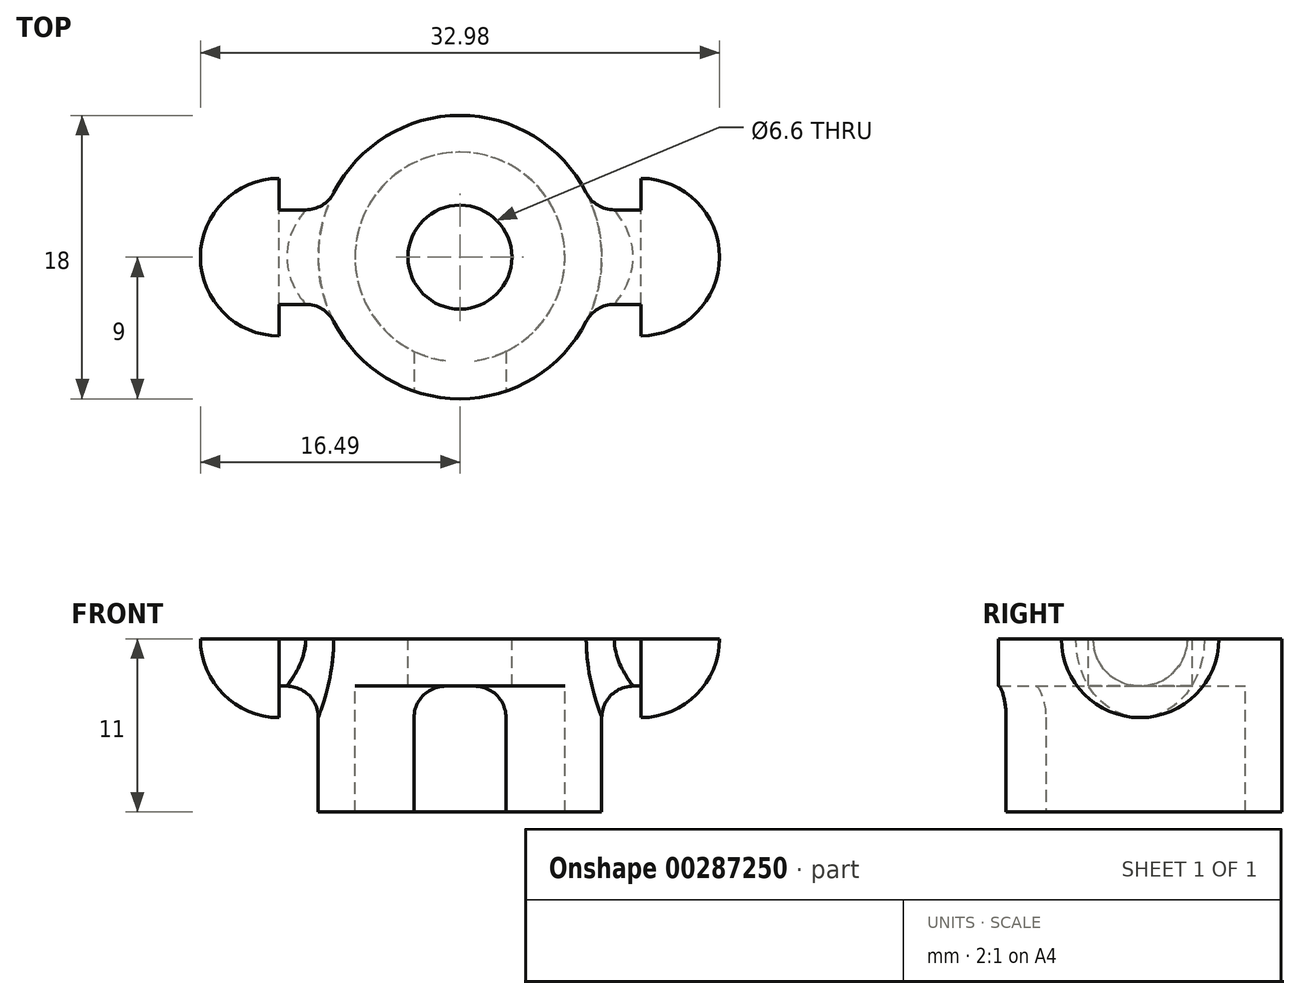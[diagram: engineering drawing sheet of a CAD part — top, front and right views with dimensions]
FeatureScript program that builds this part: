
annotation { "Feature Type Name" : "Feature", "Feature Type Description" : "" }
export const myFeature = defineFeature(function(context is Context, id is Id, definition is map)
    precondition{}
    {
        {
            var Q0;
            Q0=qCreatedBy(makeId("Front.planeOp"),FACE);
            var sketch = newSketch(context, id + "F0", { "sketchPlane" : qUnion([Q0])});
            skLineSegment(sketch, "E0", {"start": v(3.3, 8) * mm, "end": v(3.3, 11) * mm});
            skLineSegment(sketch, "E1", {"start": v(3.3, 11) * mm, "end": v(9, 11) * mm});
            skLineSegment(sketch, "E2", {"start": v(9, 11) * mm, "end": v(9, 0) * mm});
            skLineSegment(sketch, "E3", {"start": v(9, 0) * mm, "end": v(6.67, 0) * mm});
            skLineSegment(sketch, "E4", {"start": v(6.67, 0) * mm, "end": v(6.67, 8) * mm});
            skLineSegment(sketch, "E5", {"start": v(6.67, 8) * mm, "end": v(3.3, 8) * mm});
            skLineSegment(sketch, "E6", {"start": v(0, 15.16) * mm, "end": v(0, -2.88) * mm, "construction": true});
            skSolve(sketch);
        }
        {
            var Q0;
            Q0=makeQuery(id+"F0.imprint","IMPRINT",FACE,{"disambiguationData":[TD([[makeQuery(id+"F0.imprint","IMPRINT",EDGE,{"derivedFrom":sQuery(id+"F0.wireOp",EDGE,"E0")}),-1.0]])]});
            var Q1;
            Q1=sQuery(id+"F0.wireOp",EDGE,"E6");
            revolve(context, id + "F1", {"surfaceOperationType" : NewSurfaceOperationType.NEW, "entities" : qUnion([Q0]), "axis" : qUnion([Q1]), "revolveType" : RevolveType.FULL});
        }
        {
            var Q0;
            Q0=makeQuery(id+"F1.opRevolve","SWEPT_FACE",FACE,{"disambiguationData":[OSD([sQuery(id+"F0.wireOp",EDGE,"E3")])]});
            var sketch = newSketch(context, id + "F2", { "sketchPlane" : qUnion([Q0])});
            skPoint(sketch, "E7.center", {"position": v(0, 0) * mm});
            skLineSegment(sketch, "E8.bottom", {"start": v(-2.92, 6) * mm, "end": v(2.92, 6) * mm});
            skLineSegment(sketch, "E8.top", {"start": v(-2.92, 11.84) * mm, "end": v(2.92, 11.84) * mm});
            skLineSegment(sketch, "E8.left", {"start": v(-2.92, 6) * mm, "end": v(-2.92, 11.84) * mm});
            skLineSegment(sketch, "E8.right", {"start": v(2.92, 6) * mm, "end": v(2.92, 11.84) * mm});
            skSolve(sketch);
        }
        {
            var Q0;
            {var subQ1=sQuery(id+"F2.wireOp",EDGE,"w6xnzoT7-bgPk-9Upf-5AAb-UhEphA4lJJCf.bottom");var subQ2=sQuery(id+"F0.wireOp",EDGE,"E3");var subQ5=makeQuery(id+"F1.opRevolve","SWEPT_EDGE",EDGE,{"disambiguationData":[OSD([sQuery(id+"F0.wireOp",EDGE,"E2"),subQ2])]});var subQ6=makeQuery(id+"F2.imprint","INTERSECT",VERTEX,{"derivedFrom":[subQ5,subQ1]});Q0=makeQuery(id+"F2.imprint","IMPRINT",FACE,{"disambiguationData":[TD([[makeQuery(id+"F2.imprint","IMPRINT",EDGE,{"disambiguationData":[TD([[subQ6,1.0]])],"derivedFrom":subQ1}),1.0]])]});}
            var Q1;
            {var subQ0=sQuery(id+"F2.wireOp",EDGE,"E8.left");var subQ2=sQuery(id+"F0.wireOp",EDGE,"E3");var subQ5=makeQuery(id+"F1.opRevolve","SWEPT_EDGE",EDGE,{"disambiguationData":[OSD([sQuery(id+"F0.wireOp",EDGE,"E2"),subQ2])]});var subQ6=makeQuery(id+"F2.imprint","INTERSECT",VERTEX,{"derivedFrom":[subQ5,subQ0]});Q1=makeQuery(id+"F2.imprint","IMPRINT",FACE,{"disambiguationData":[TD([[makeQuery(id+"F2.imprint","IMPRINT",EDGE,{"disambiguationData":[TD([[subQ6,1.0]])],"derivedFrom":subQ0}),-1.0]])]});}
            var Q2;
            Q2=makeQuery(id+"F1.opRevolve","SWEPT_FACE",FACE,{"disambiguationData":[OSD([sQuery(id+"F0.wireOp",EDGE,"E5")])]});
            extrude(context, id + "F3", {"entities" : qUnion([Q0, Q1]), "operationType" : NewBodyOperationType.REMOVE, "endBound" : BoundingType.UP_TO_SURFACE, "oppositeDirection" : true, "depth" : 25 * mm, "endBoundEntityFace" : qUnion([Q2]), "offsetDistance" : 25 * mm});
        }
        {
            var Q0;
            Q0=makeQuery(id+"F1.opRevolve","SWEPT_FACE",FACE,{"disambiguationData":[OSD([sQuery(id+"F0.wireOp",EDGE,"E1")])]});
            var sketch = newSketch(context, id + "F4", { "sketchPlane" : qUnion([Q0])});
            skLineSegment(sketch, "E9.bottom", {"start": v(8.49, 3) * mm, "end": v(11.49, 3) * mm});
            skLineSegment(sketch, "E9.right", {"start": v(11.49, 5) * mm, "end": v(11.49, 3) * mm});
            skArc(sketch, "E10", {"start": v(16.49, 0) * mm, "mid": v(15.02, 3.54) * mm, "end": v(11.49, 5) * mm});
            skLineSegment(sketch, "E11", {"start": v(9, 0) * mm, "end": v(16.49, 0) * mm});
            skPoint(sketch, "E12.orphan", {"position": v(9, 0) * mm});
            skArc(sketch, "E13.0", {"start": v(9, 0) * mm, "mid": v(8.87, 1.52) * mm, "end": v(8.49, 3) * mm});
            skArc(sketch, "E14.MirrorCS", {"start": v(-9, 0) * mm, "mid": v(-8.87, 1.52) * mm, "end": v(-8.49, 3) * mm});
            skArc(sketch, "E15.MirrorCS", {"start": v(-16.49, 0) * mm, "mid": v(-15.02, 3.54) * mm, "end": v(-11.49, 5) * mm});
            skLineSegment(sketch, "E16.MirrorCS", {"start": v(-11.49, 5) * mm, "end": v(-11.49, 3) * mm});
            skLineSegment(sketch, "E17.MirrorCS", {"start": v(-9, 0) * mm, "end": v(-16.49, 0) * mm});
            skPoint(sketch, "E18.MirrorP", {"position": v(-9, 0) * mm});
            skLineSegment(sketch, "E19.MirrorCS", {"start": v(-8.49, 3) * mm, "end": v(-11.49, 3) * mm});
            skSolve(sketch);
        }
        {
            var Q0;
            Q0=makeQuery(id+"F4.imprint","IMPRINT",FACE,{"disambiguationData":[TD([[makeQuery(id+"F4.imprint","IMPRINT",EDGE,{"derivedFrom":sQuery(id+"F4.wireOp",EDGE,"E14.MirrorCS")}),-1.0]])]});
            var Q1;
            Q1=sQuery(id+"F4.wireOp",EDGE,"E17.MirrorCS");
            revolve(context, id + "F5", {"operationType" : NewBodyOperationType.ADD, "surfaceOperationType" : NewSurfaceOperationType.NEW, "entities" : qUnion([Q0]), "axis" : qUnion([Q1]), "revolveType" : RevolveType.ONE_DIRECTION, "angle" : 180 * degree});
        }
        {
            var Q0;
            Q0=makeQuery(id+"F4.imprint","IMPRINT",FACE,{"disambiguationData":[TD([[makeQuery(id+"F4.imprint","IMPRINT",EDGE,{"derivedFrom":sQuery(id+"F4.wireOp",EDGE,"E9.bottom")}),-1.0]])]});
            var Q1;
            Q1=sQuery(id+"F4.wireOp",EDGE,"E11");
            revolve(context, id + "F6", {"operationType" : NewBodyOperationType.ADD, "surfaceOperationType" : NewSurfaceOperationType.NEW, "entities" : qUnion([Q0]), "axis" : qUnion([Q1]), "revolveType" : RevolveType.ONE_DIRECTION, "oppositeDirection" : true, "angle" : 180 * degree});
        }
        {
            var Q0;
            Q0=makeQuery(id+"F5.boolean.opBoolean","INTERSECT",EDGE,{"derivedFrom":[makeQuery(id+"F1.opRevolve","SWEPT_FACE",FACE,{"disambiguationData":[OSD([sQuery(id+"F0.wireOp",EDGE,"E2")])]}),makeQuery(id+"F5.opRevolve","SWEPT_FACE",FACE,{"disambiguationData":[OSD([sQuery(id+"F4.wireOp",EDGE,"E19.MirrorCS")])]})]});
            var Q1;
            Q1=makeQuery(id+"F6.boolean.opBoolean","INTERSECT",EDGE,{"derivedFrom":[makeQuery(id+"F1.opRevolve","SWEPT_FACE",FACE,{"disambiguationData":[OSD([sQuery(id+"F0.wireOp",EDGE,"E2")])]}),makeQuery(id+"F6.opRevolve","SWEPT_FACE",FACE,{"disambiguationData":[OSD([sQuery(id+"F4.wireOp",EDGE,"E9.bottom")])]})]});
            var Q2;
            Q2=makeQuery(id+"F3.boolean.opBoolean","COPY",EDGE,{"derivedFrom":makeQuery(id+"F3.opExtrude","CAP_EDGE",EDGE,{"disambiguationData":[OSD([sQuery(id+"F2.wireOp",EDGE,"E8.left")])],"isStart":false})});
            var Q3;
            Q3=makeQuery(id+"F3.boolean.opBoolean","COPY",EDGE,{"derivedFrom":makeQuery(id+"F3.opExtrude","CAP_EDGE",EDGE,{"disambiguationData":[OSD([sQuery(id+"F2.wireOp",EDGE,"E8.right")])],"isStart":false})});
            fillet(context, id + "F7", {"entities" : qUnion([Q0, Q1, Q2, Q3]), "radius" : 2 * mm, "tangentPropagation" : true, "allowEdgeOverflow" : false});
        }
    });
